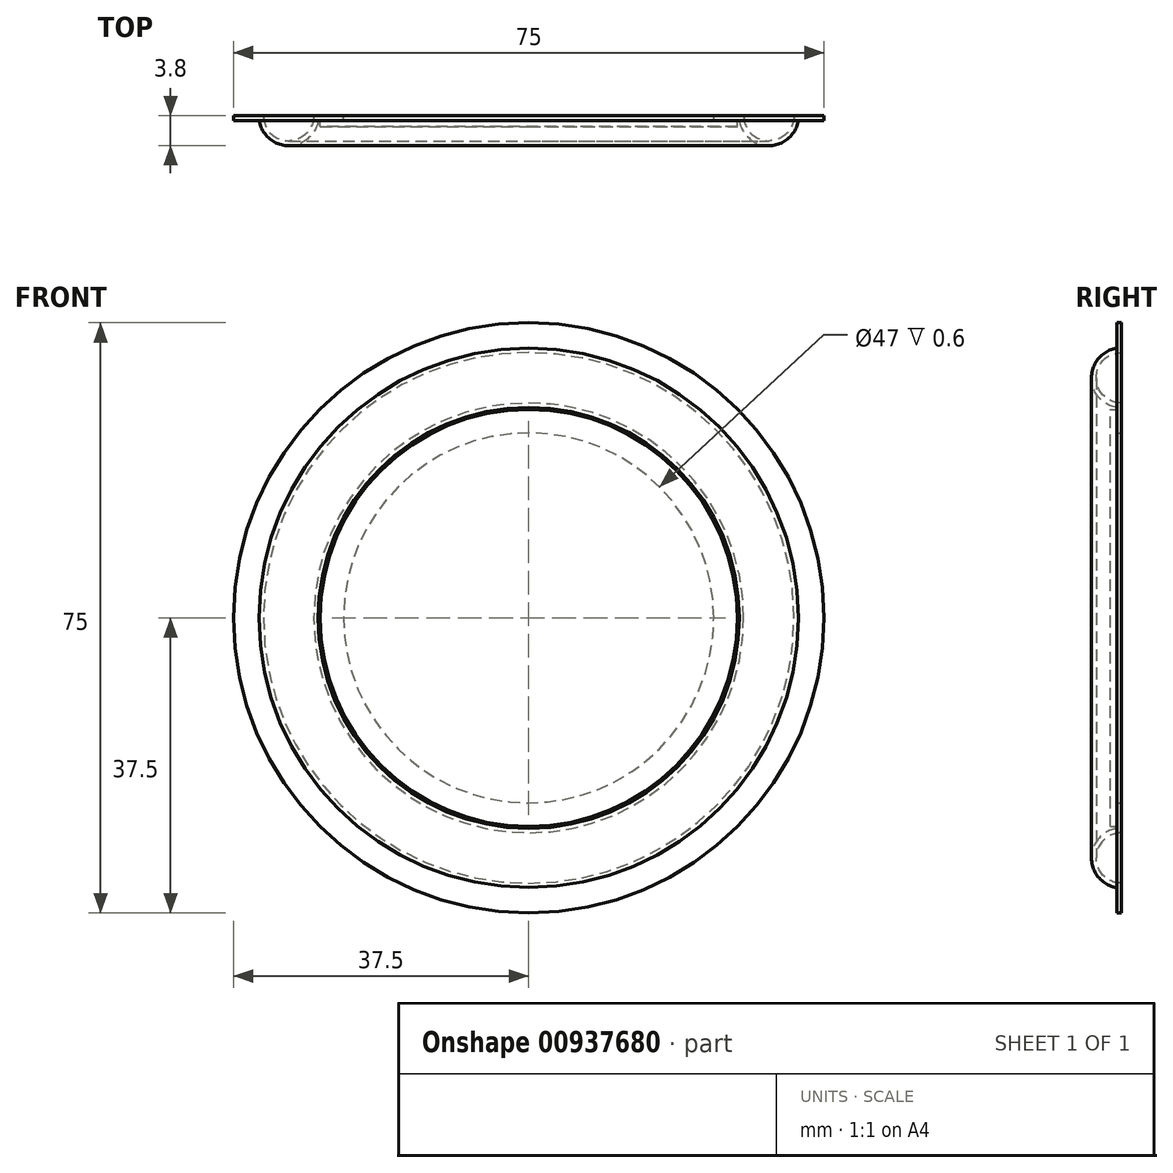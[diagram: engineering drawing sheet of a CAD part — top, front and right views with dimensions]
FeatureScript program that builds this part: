
annotation { "Feature Type Name" : "Feature", "Feature Type Description" : "" }
export const myFeature = defineFeature(function(context is Context, id is Id, definition is map)
    precondition{}
    {
        {
            var Q0;
            Q0=qCreatedBy(makeId("Front.planeOp"),FACE);
            var sketch = newSketch(context, id + "F0", { "sketchPlane" : qUnion([Q0])});
            skCircle(sketch, "E0", {"center": v(0, 0) * mm, "radius": 26.5 * mm});
            skSolve(sketch);
        }
        {
            var Q0;
            Q0 = qSketchRegion(id + "F0", true);
            extrude(context, id + "F1", {"entities" : qUnion([Q0]), "depth" : 0.8 * mm, "offsetDistance" : 25 * mm});
        }
        {
            var Q0;
            Q0=qCreatedBy(makeId("Top.planeOp"),FACE);
            var sketch = newSketch(context, id + "F2", { "sketchPlane" : qUnion([Q0])});
            skLineSegment(sketch, "E1", {"start": v(23.5, 0) * mm, "end": v(23.5, 0.6) * mm});
            skLineSegment(sketch, "E2", {"start": v(23.5, 0.6) * mm, "end": v(27.3, 0.6) * mm});
            skArc(sketch, "E3", {"start": v(27.3, 0.6) * mm, "mid": v(30.5, -2.6) * mm, "end": v(33.7, 0.6) * mm});
            skArc(sketch, "E4.0", {"start": v(26.75, 0) * mm, "mid": v(30.5, -3.2) * mm, "end": v(34.25, 0) * mm});
            skLineSegment(sketch, "E5", {"start": v(23.5, 0) * mm, "end": v(26.75, 0) * mm});
            skLineSegment(sketch, "E6", {"start": v(33.7, 0.6) * mm, "end": v(37.5, 0.6) * mm});
            skLineSegment(sketch, "E7", {"start": v(37.5, 0.6) * mm, "end": v(37.5, 0.6) * mm});
            skLineSegment(sketch, "E8", {"start": v(37.5, 0.6) * mm, "end": v(37.5, 0) * mm});
            skLineSegment(sketch, "E9", {"start": v(37.5, 0) * mm, "end": v(34.25, 0) * mm});
            skLineSegment(sketch, "E10", {"start": v(0, -8.14) * mm, "end": v(0, 7.1) * mm, "construction": true});
            skSolve(sketch);
        }
        {
            var Q0;
            Q0=makeQuery(id+"F2.imprint","IMPRINT",FACE,{"disambiguationData":[TD([[makeQuery(id+"F2.imprint","IMPRINT",EDGE,{"derivedFrom":sQuery(id+"F2.wireOp",EDGE,"E1")}),-1.0]])]});
            var Q1;
            Q1=makeQuery(id+"F1.opExtrude","CAP_EDGE",EDGE,{"disambiguationData":[OSD([sQuery(id+"F0.wireOp",EDGE,"E0")])],"isStart":false});
            revolve(context, id + "F3", {"surfaceOperationType" : NewSurfaceOperationType.NEW, "entities" : qUnion([Q0]), "axis" : qUnion([Q1]), "revolveType" : RevolveType.FULL});
        }
    });
